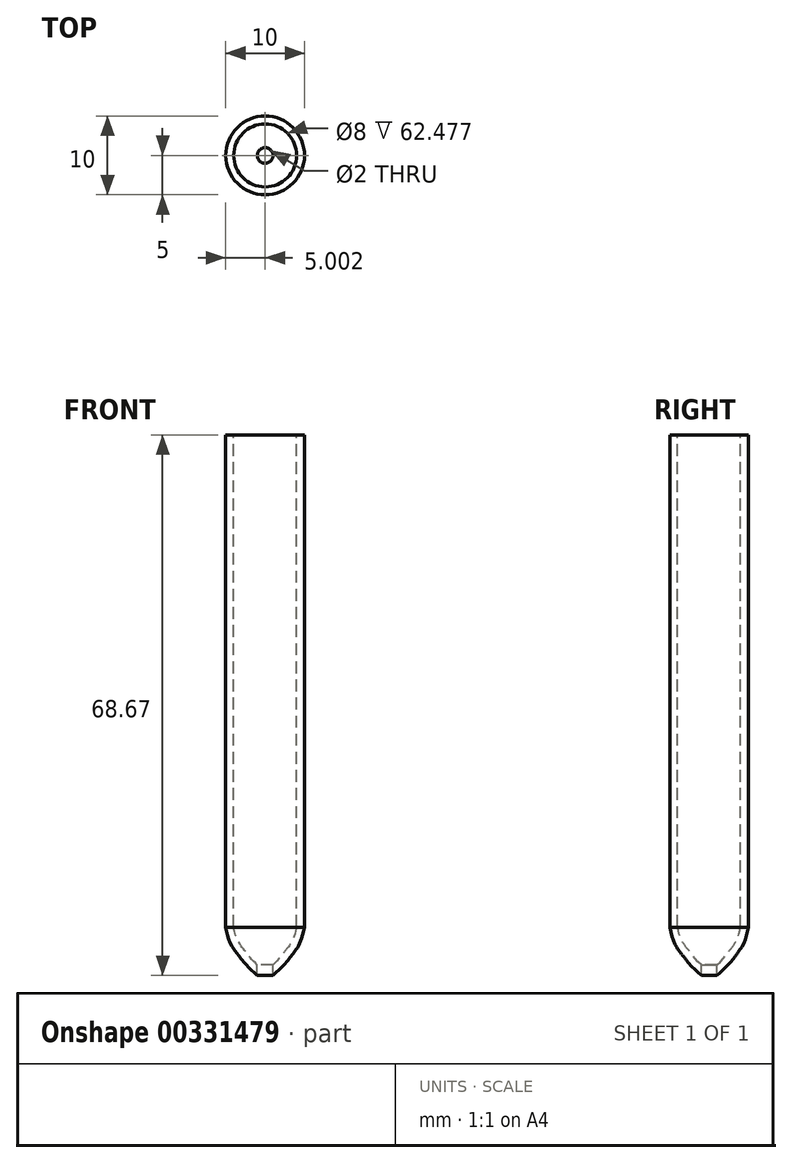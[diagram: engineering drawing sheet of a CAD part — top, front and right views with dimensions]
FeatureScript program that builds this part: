
annotation { "Feature Type Name" : "Feature", "Feature Type Description" : "" }
export const myFeature = defineFeature(function(context is Context, id is Id, definition is map)
    precondition{}
    {
        {
            var Q0;
            Q0=qCreatedBy(makeId("Front.planeOp"),FACE);
            var sketch = newSketch(context, id + "F0", { "sketchPlane" : qUnion([Q0])});
            skLineSegment(sketch, "E0", {"start": v(4.98, 52.5) * mm, "end": v(4.98, -10.06) * mm});
            skLineSegment(sketch, "E1.0", {"start": v(-0.02, 52.5) * mm, "end": v(-0.02, -16.17) * mm});
            skFitSpline(sketch, "E2", {"points": [v(4.98, -10.06) * mm, v(3.44, -13.51) * mm, v(0.98, -16.17) * mm], "startDerivative": vector(-2.34, -12.57) * mm, "endDerivative": vector(-9.92, -8.96) * mm});
            skLineSegment(sketch, "E3", {"start": v(3.98, 52.5) * mm, "end": v(4.98, 52.5) * mm});
            skLineSegment(sketch, "E4.0", {"start": v(0.98, -14.8) * mm, "end": v(0.98, -16.17) * mm});
            skFitSpline(sketch, "E5.0", {"points": [v(4, -9.88) * mm, v(3.9, -10.37) * mm, v(3.7, -11.15) * mm, v(3.43, -11.78) * mm, v(3.2, -12.16) * mm, v(3.04, -12.4) * mm, v(2.89, -12.6) * mm, v(2.76, -12.75) * mm, v(2.67, -12.88) * mm, v(2.57, -13) * mm, v(2.44, -13.17) * mm, v(2.3, -13.36) * mm, v(2.12, -13.6) * mm, v(1.83, -13.94) * mm, v(1.35, -14.46) * mm, v(0.71, -15.07) * mm, v(0.31, -15.43) * mm]});
            skLineSegment(sketch, "E6.0", {"start": v(3.98, 52.5) * mm, "end": v(3.98, -10.06) * mm});
            skSolve(sketch);
        }
        {
            var Q0;
            Q0=makeQuery(id+"F0.imprint","IMPRINT",FACE,{"disambiguationData":[TD([[makeQuery(id+"F0.imprint","IMPRINT",EDGE,{"derivedFrom":sQuery(id+"F0.wireOp",EDGE,"E0")}),-1.0]])]});
            var Q1;
            Q1=sQuery(id+"F0.wireOp",EDGE,"E1.0");
            revolve(context, id + "F1", {"entities" : qUnion([Q0]), "axis" : qUnion([Q1]), "revolveType" : RevolveType.FULL});
        }
    });
